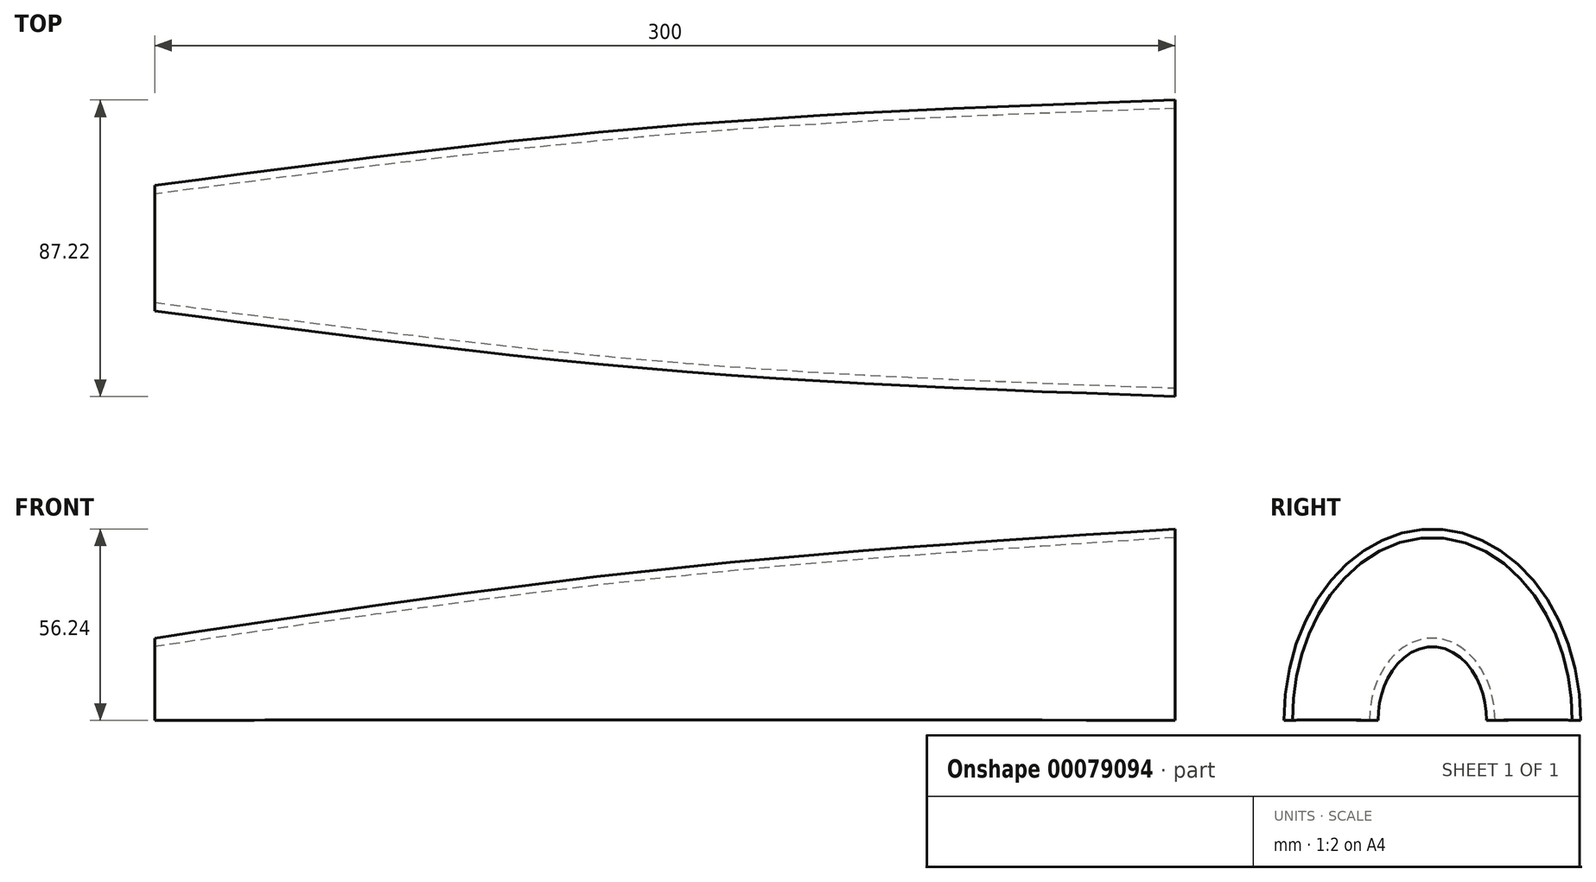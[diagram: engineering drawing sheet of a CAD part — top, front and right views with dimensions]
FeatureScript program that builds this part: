
annotation { "Feature Type Name" : "Feature", "Feature Type Description" : "" }
export const myFeature = defineFeature(function(context is Context, id is Id, definition is map)
    precondition{}
    {
        {
            var Q0;
            Q0=qCreatedBy(makeId("Right.planeOp"),FACE);
            cPlane(context, id + "F0", {"entities" : qUnion([Q0]), "cplaneType" : CPlaneType.OFFSET, "offset" : 150 * mm, "oppositeDirection" : true, "width" : 150 * mm, "height" : 150 * mm});
        }
        {
            var Q0;
            Q0=qCreatedBy(makeId("Right.planeOp"),FACE);
            cPlane(context, id + "F1", {"entities" : qUnion([Q0]), "cplaneType" : CPlaneType.OFFSET, "offset" : 150 * mm, "width" : 150 * mm, "height" : 150 * mm});
        }
        {
            var Q0;
            Q0=qCreatedBy(id+"F0.planeOp",FACE);
            var sketch = newSketch(context, id + "F2", { "sketchPlane" : qUnion([Q0])});
            skEllipticalArc(sketch, "E0", {});
            skLineSegment(sketch, "E1", {"start": v(-18.46, 0) * mm, "end": v(18.46, 0) * mm});
            const initialGuessF2  = {"E0": [0, 0, 0, 1, 0.024175889790058136, 0.018455413530350726, 4.71238898038469, 1.5707963267948966]};
            skSetInitialGuess(sketch, initialGuessF2);
            skSolve(sketch);
        }
        {
            var Q0;
            Q0=qCreatedBy(makeId("Right.planeOp"),FACE);
            var sketch = newSketch(context, id + "F3", { "sketchPlane" : qUnion([Q0])});
            skEllipticalArc(sketch, "E2", {});
            skLineSegment(sketch, "E3", {"start": v(-35.81, 0.16) * mm, "end": v(35.81, 0.16) * mm});
            const initialGuessF3  = {"E2": [2.4242073886487914e-10, 0.00016428074692959212, 0, 1, 0.04430137947201729, 0.03581269629660675, 4.71238898038469, 1.5707963267948966]};
            skSetInitialGuess(sketch, initialGuessF3);
            skSolve(sketch);
        }
        {
            var Q0;
            Q0=qCreatedBy(id+"F1.planeOp",FACE);
            var sketch = newSketch(context, id + "F4", { "sketchPlane" : qUnion([Q0])});
            skEllipticalArc(sketch, "E4", {});
            skLineSegment(sketch, "E5", {"start": v(-43.61, 0) * mm, "end": v(43.61, 0) * mm});
            const initialGuessF4  = {"E4": [0, 0, 0, 1, 0.05623750388622284, 0.043613115393651626, 4.71238898038469, 1.5707963267948966]};
            skSetInitialGuess(sketch, initialGuessF4);
            skSolve(sketch);
        }
        {
            var Q0;
            Q0 = qSketchRegion(id + "F2", true);
            var Q1;
            Q1 = qSketchRegion(id + "F3", true);
            var Q2;
            Q2 = qSketchRegion(id + "F4", true);
            loft(context, id + "F5", {"sheetProfilesArray" : [{ "sheetProfileEntities" : qUnion([Q0]) }, { "sheetProfileEntities" : qUnion([Q1]) }, { "sheetProfileEntities" : qUnion([Q2]) }]});
        }
        {
            var Q0;
            Q0=makeQuery(id+"F5.opLoft","CAP_FACE",FACE,{"disambiguationData":[OSD([makeQuery(id+"F4.imprint","IMPRINT",FACE,{"disambiguationData":[TD([[makeQuery(id+"F4.imprint","IMPRINT",EDGE,{"derivedFrom":sQuery(id+"F4.wireOp",EDGE,"E4")}),1.0]])]})])],"isStart":true});
            var Q1;
            {var subQ0=sQuery(id+"F3.wireOp",EDGE,"E3");var subQ1=sQuery(id+"F3.wireOp",EDGE,"E2");var subQ2=sQuery(id+"F2.wireOp",EDGE,"E1");var subQ3=sQuery(id+"F2.wireOp",EDGE,"E0");Q1=makeQuery(id+"F5.opLoft","SWEPT_FACE",FACE,{"disambiguationData":[OSD([subQ3,subQ2,subQ1,subQ0]),TDD([makeQuery(id+"F2.imprint","INTERSECT",VERTEX,{"disambiguationData":[OD(0.0)],"derivedFrom":[subQ3,subQ2]}),makeQuery(id+"F2.imprint","INTERSECT",VERTEX,{"disambiguationData":[OD(1.0)],"derivedFrom":[subQ3,subQ2]}),makeQuery(id+"F2.imprint","IMPRINT",EDGE,{"derivedFrom":subQ2}),makeQuery(id+"F3.imprint","INTERSECT",VERTEX,{"disambiguationData":[OD(0.0)],"derivedFrom":[subQ1,subQ0]}),makeQuery(id+"F3.imprint","INTERSECT",VERTEX,{"disambiguationData":[OD(1.0)],"derivedFrom":[subQ1,subQ0]}),makeQuery(id+"F3.imprint","IMPRINT",EDGE,{"derivedFrom":subQ0})])]});}
            var Q2;
            Q2=makeQuery(id+"F5.opLoft","CAP_FACE",FACE,{"disambiguationData":[OSD([makeQuery(id+"F2.imprint","IMPRINT",FACE,{"disambiguationData":[TD([[makeQuery(id+"F2.imprint","IMPRINT",EDGE,{"derivedFrom":sQuery(id+"F2.wireOp",EDGE,"E0")}),1.0]])]})])],"isStart":true});
            shell(context, id + "F6", {"entities" : qUnion([Q0, Q1, Q2]), "thickness" : 2.5 * mm});
        }
    });
